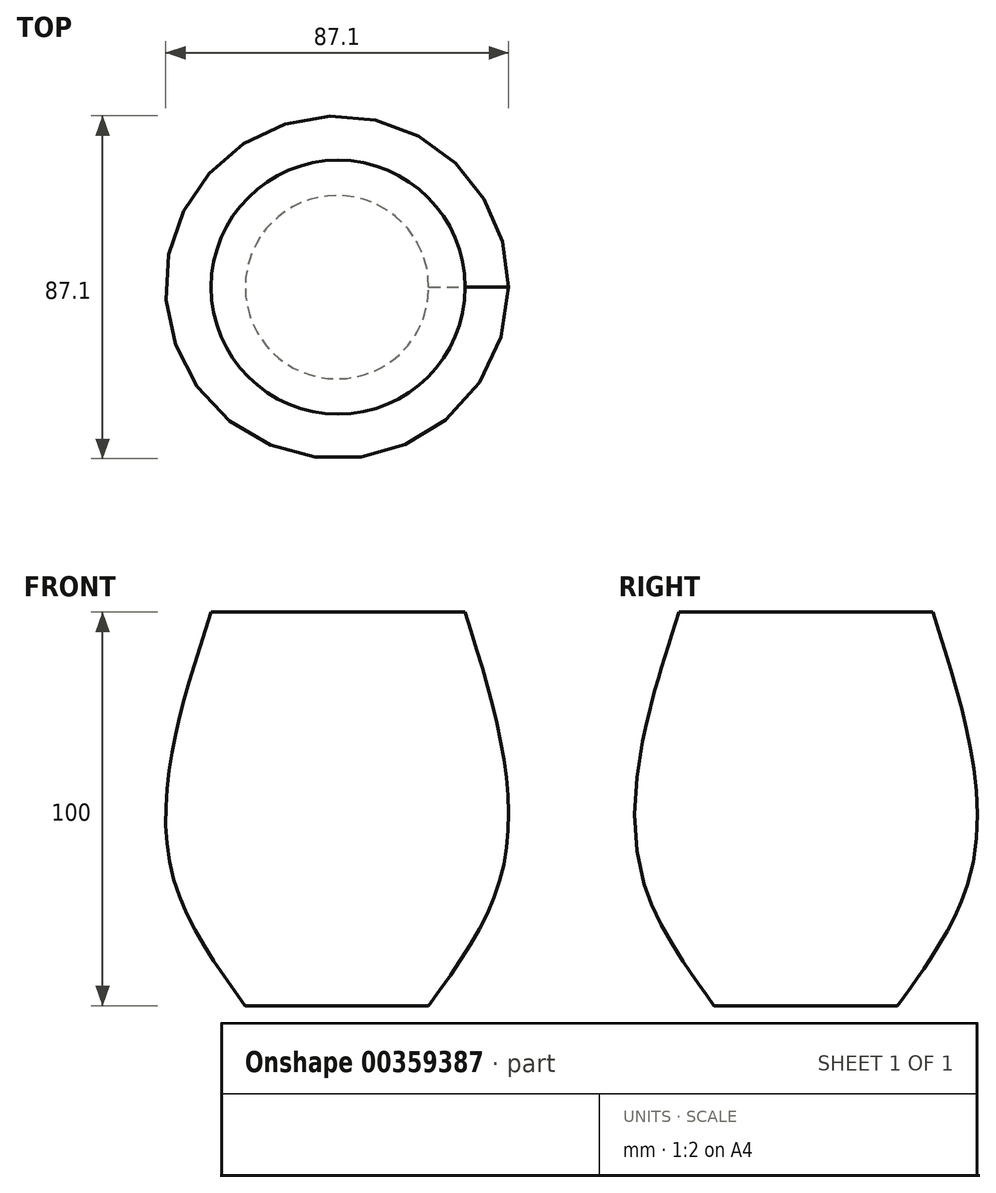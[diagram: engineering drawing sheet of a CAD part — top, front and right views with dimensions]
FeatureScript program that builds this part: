
annotation { "Feature Type Name" : "Feature", "Feature Type Description" : "" }
export const myFeature = defineFeature(function(context is Context, id is Id, definition is map)
    precondition{}
    {
        {
            var Q0;
            Q0=qCreatedBy(makeId("Front.planeOp"),FACE);
            var sketch = newSketch(context, id + "F0", { "sketchPlane" : qUnion([Q0])});
            skFitSpline(sketch, "E0", {"points": [v(-17.06, 0) * mm, v(-33.06, 28.66) * mm, v(-22.13, 57.73) * mm, v(-29.06, 78.8) * mm], "startDerivative": vector(-69.43, 78.3) * mm, "endDerivative": vector(-41.67, 68.5) * mm});
            skLineSegment(sketch, "E1", {"start": v(0, 0) * mm, "end": v(0, 91.6) * mm, "construction": true});
            skSolve(sketch);
        }
        {
            var Q0;
            Q0=sQuery(id+"F0.wireOp",EDGE,"E0");
            var Q1;
            Q1=sQuery(id+"F0.wireOp",EDGE,"E1");
            revolve(context, id + "F1", {"bodyType" : ToolBodyType.SURFACE, "surfaceEntities" : qUnion([Q0]), "axis" : qUnion([Q1]), "revolveType" : RevolveType.FULL});
        }
        {
            var Q0;
            Q0=qCreatedBy(makeId("Top.planeOp"),FACE);
            var sketch = newSketch(context, id + "F2", { "sketchPlane" : qUnion([Q0])});
            skCircle(sketch, "E2", {"center": v(100.05, 0) * mm, "radius": 23.3 * mm});
            skSolve(sketch);
        }
        {
            var Q0;
            Q0=qCreatedBy(makeId("Top.planeOp"),FACE);
            cPlane(context, id + "F3", {"entities" : qUnion([Q0]), "cplaneType" : CPlaneType.OFFSET, "offset" : 30 * mm, "width" : 150 * mm, "height" : 150 * mm});
        }
        {
            var Q0;
            Q0=qCreatedBy(makeId("Top.planeOp"),FACE);
            cPlane(context, id + "F4", {"entities" : qUnion([Q0]), "cplaneType" : CPlaneType.OFFSET, "offset" : 100 * mm, "width" : 150 * mm, "height" : 150 * mm});
        }
        {
            var Q0;
            Q0=qCreatedBy(id+"F3.planeOp",FACE);
            var sketch = newSketch(context, id + "F5", { "sketchPlane" : qUnion([Q0])});
            skCircle(sketch, "E3", {"center": v(100.02, 0) * mm, "radius": 40.82 * mm});
            skSolve(sketch);
        }
        {
            var Q0;
            Q0=qCreatedBy(id+"F4.planeOp",FACE);
            var sketch = newSketch(context, id + "F6", { "sketchPlane" : qUnion([Q0])});
            skCircle(sketch, "E4", {"center": v(100.33, 0) * mm, "radius": 32.26 * mm});
            skSolve(sketch);
        }
        {
            var Q0;
            Q0=makeQuery(id+"F2.imprint","IMPRINT",FACE,{"disambiguationData":[TD([[makeQuery(id+"F2.imprint","IMPRINT",EDGE,{"derivedFrom":sQuery(id+"F2.wireOp",EDGE,"E2")}),1.0]])]});
            var Q1;
            Q1=makeQuery(id+"F5.imprint","IMPRINT",FACE,{"disambiguationData":[TD([[makeQuery(id+"F5.imprint","IMPRINT",EDGE,{"derivedFrom":sQuery(id+"F5.wireOp",EDGE,"E3")}),1.0]])]});
            var Q2;
            Q2=makeQuery(id+"F6.imprint","IMPRINT",FACE,{"disambiguationData":[TD([[makeQuery(id+"F6.imprint","IMPRINT",EDGE,{"derivedFrom":sQuery(id+"F6.wireOp",EDGE,"E4")}),1.0]])]});
            loft(context, id + "F7", {"sheetProfilesArray" : [{ "sheetProfileEntities" : qUnion([Q0]) }, { "sheetProfileEntities" : qUnion([Q1]) }, { "sheetProfileEntities" : qUnion([Q2]) }]});
        }
    });
